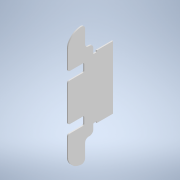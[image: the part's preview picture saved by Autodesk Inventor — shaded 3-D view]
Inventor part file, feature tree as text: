
AUTODESK INVENTOR PART (.ipt)
format: ipt  version: 2022 (Build 260153000, 153)  size: 281,088 bytes
history: native  units: mm
features: reference x16, other x8, extrude x4, sketch x4, fillet x3, projected_geometry x2
ambient origin geometry x8: Origin, YZ Plane, XZ Plane, XY Plane, X Axis, Y Axis, Z Axis, Center Point
bodies: Body1 (feature_tree)
feature tree (37):
  other  "Твердое тело1"
  extrude  "Выдавливание1"  Depth=80.0mm
  extrude  "Выдавливание2"  Depth=50.0mm
  extrude  "Выдавливание4"  Depth=1.2mm TaperAngle=0.0deg
  fillet  "Сопряжение3"  Radius=0.3mm
  extrude  "Выдавливание5"  Depth=10.0mm TaperAngle=0.0deg
  fillet  "Сопряжение4"  Radius=0.3mm
  fillet  "Сопряжение5"  Radius=0.3mm
  sketch  "Эскиз1"
  reference  "Ссылка1"
  reference  "Ссылка2"
  reference  "Ссылка3"
  sketch  "Эскиз2"
  sketch  "Эскиз4"
  reference  "Ссылка15"
  reference  "Ссылка16"
  reference  "Ссылка23"
  reference  "Ссылка24"
  reference  "Ссылка25"
  reference  "Ссылка26"
  reference  "Ссылка27"
  reference  "Ссылка28"
  projected_geometry  "Спроецированная петля1"
  reference  "Ссылка29"
  reference  "Ссылка30"
  reference  "Ссылка31"
  reference  "Ссылка32"
  sketch  "Эскиз5"
  projected_geometry  "Спроецированная петля2"
  reference  "Ссылка33"
  other  "<userpath>\Documents\Git\MZCAT_2024\MZCAT_3.iam"
  other  "MZCAT_3.iam"
  other  "CAT_protector:1"
  other  "commutationCATboard:1"
  other  "akkum_cup:1"
  other  "push-fit:1"
  other  "push-fit:2"
